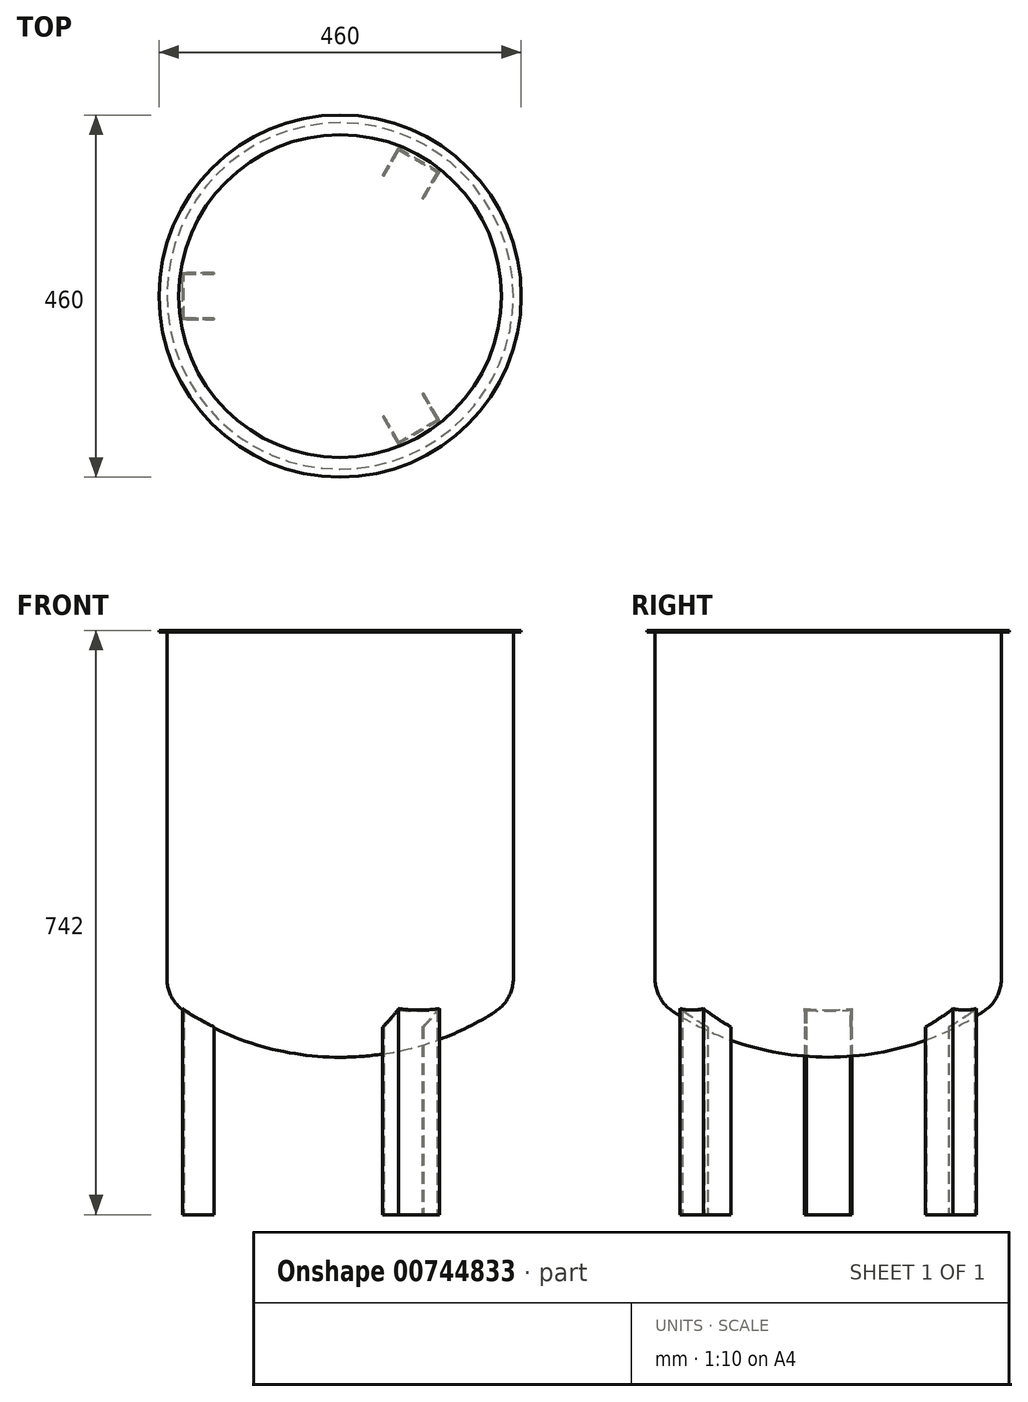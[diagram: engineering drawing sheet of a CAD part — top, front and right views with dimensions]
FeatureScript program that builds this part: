
annotation { "Feature Type Name" : "Feature", "Feature Type Description" : "" }
export const myFeature = defineFeature(function(context is Context, id is Id, definition is map)
    precondition{}
    {
        {
            var Q0;
            Q0=qCreatedBy(makeId("Front.planeOp"),FACE);
            var sketch = newSketch(context, id + "F0", { "sketchPlane" : qUnion([Q0])});
            skLineSegment(sketch, "E0", {"start": v(-220, 100) * mm, "end": v(-220, 540) * mm});
            skArc(sketch, "E1", {"start": v(0, 640) * mm, "mid": v(-102.7, 625.2) * mm, "end": v(-197.07, 582.04) * mm});
            skLineSegment(sketch, "E2", {"start": v(0, 640) * mm, "end": v(58.23, 640) * mm, "construction": true});
            skPoint(sketch, "E3.visualSharp", {"position": v(-220, 566) * mm});
            skArc(sketch, "E3.filletArc", {"start": v(-197.07, 582.04) * mm, "mid": v(-213.9, 563.94) * mm, "end": v(-220, 540) * mm});
            skArc(sketch, "E4", {"start": v(-197.07, 57.96) * mm, "mid": v(-102.7, 14.8) * mm, "end": v(0, 0) * mm});
            skPoint(sketch, "E5.visualSharp", {"position": v(-220, 74) * mm});
            skArc(sketch, "E5.filletArc", {"start": v(-220, 100) * mm, "mid": v(-213.9, 76.06) * mm, "end": v(-197.07, 57.96) * mm});
            skLineSegment(sketch, "E6", {"start": v(0, 0) * mm, "end": v(49.75, 0) * mm, "construction": true});
            skLineSegment(sketch, "E7", {"start": v(0, 640) * mm, "end": v(0, 0) * mm});
            skLineSegment(sketch, "E8", {"start": v(0, 640) * mm, "end": v(0, 722.44) * mm, "construction": true});
            skSolve(sketch);
        }
        {
            var Q0;
            Q0=makeQuery(id+"F0.imprint","IMPRINT",FACE,{"disambiguationData":[TD([[makeQuery(id+"F0.imprint","IMPRINT",EDGE,{"derivedFrom":sQuery(id+"F0.wireOp",EDGE,"E0")}),-1.0]])]});
            var Q1;
            Q1=sQuery(id+"F0.wireOp",EDGE,"E8");
            revolve(context, id + "F1", {"surfaceOperationType" : NewSurfaceOperationType.NEW, "entities" : qUnion([Q0]), "axis" : qUnion([Q1]), "revolveType" : RevolveType.FULL});
        }
        {
            var Q0;
            Q0=qCreatedBy(makeId("Top.planeOp"),FACE);
            var sketch = newSketch(context, id + "F2", { "sketchPlane" : qUnion([Q0])});
            skLineSegment(sketch, "E9", {"start": v(-160, -30) * mm, "end": v(-200, -30) * mm});
            skLineSegment(sketch, "E10", {"start": v(-200, -30) * mm, "end": v(-200, 30) * mm});
            skLineSegment(sketch, "E11", {"start": v(-200, 30) * mm, "end": v(-160, 30) * mm});
            skLineSegment(sketch, "E12", {"start": v(-200, 0) * mm, "end": v(0, 0) * mm, "construction": true});
            skLineSegment(sketch, "E13.0", {"start": v(-198, 28) * mm, "end": v(-160, 28) * mm});
            skLineSegment(sketch, "E13.1", {"start": v(-198, -28) * mm, "end": v(-198, 28) * mm});
            skLineSegment(sketch, "E13.2", {"start": v(-160, -28) * mm, "end": v(-198, -28) * mm});
            skLineSegment(sketch, "E14", {"start": v(-160, -28) * mm, "end": v(-160, -30) * mm});
            skLineSegment(sketch, "E15", {"start": v(-160, 30) * mm, "end": v(-160, 28) * mm});
            skLineSegment(sketch, "E16.1.0", {"start": v(104.25, -124.56) * mm, "end": v(123.25, -157.47) * mm});
            skLineSegment(sketch, "E16.1.1", {"start": v(123.25, -157.47) * mm, "end": v(74.75, -185.47) * mm});
            skLineSegment(sketch, "E16.1.2", {"start": v(74.75, -185.47) * mm, "end": v(55.75, -152.56) * mm});
            skLineSegment(sketch, "E16.1.3", {"start": v(125.98, -158.2) * mm, "end": v(74.02, -188.2) * mm});
            skLineSegment(sketch, "E16.1.4", {"start": v(74.02, -188.2) * mm, "end": v(54.02, -153.56) * mm});
            skLineSegment(sketch, "E16.1.5", {"start": v(105.98, -123.56) * mm, "end": v(125.98, -158.2) * mm});
            skLineSegment(sketch, "E16.1.6", {"start": v(54.02, -153.56) * mm, "end": v(55.75, -152.56) * mm});
            skLineSegment(sketch, "E16.1.7", {"start": v(104.25, -124.56) * mm, "end": v(105.98, -123.56) * mm});
            skLineSegment(sketch, "E16.2.0", {"start": v(55.75, 152.56) * mm, "end": v(74.75, 185.47) * mm});
            skLineSegment(sketch, "E16.2.1", {"start": v(74.75, 185.47) * mm, "end": v(123.25, 157.47) * mm});
            skLineSegment(sketch, "E16.2.2", {"start": v(123.25, 157.47) * mm, "end": v(104.25, 124.56) * mm});
            skLineSegment(sketch, "E16.2.3", {"start": v(74.02, 188.2) * mm, "end": v(125.98, 158.2) * mm});
            skLineSegment(sketch, "E16.2.4", {"start": v(125.98, 158.2) * mm, "end": v(105.98, 123.56) * mm});
            skLineSegment(sketch, "E16.2.5", {"start": v(54.02, 153.56) * mm, "end": v(74.02, 188.2) * mm});
            skLineSegment(sketch, "E16.2.6", {"start": v(105.98, 123.56) * mm, "end": v(104.25, 124.56) * mm});
            skLineSegment(sketch, "E16.2.7", {"start": v(55.75, 152.56) * mm, "end": v(54.02, 153.56) * mm});
            skPoint(sketch, "E16.center", {"position": v(0, 0) * mm});
            skSolve(sketch);
        }
        {
            var Q0;
            Q0=qSketchRegion(id+"F2",true);
            var Q1;
            Q1=makeQuery(id+"F1.opRevolve","SWEPT_BODY",BODY,{"disambiguationData":[OSD([sQuery(id+"F0.wireOp",EDGE,"E0"),sQuery(id+"F0.wireOp",EDGE,"E1"),sQuery(id+"F0.wireOp",EDGE,"E3.filletArc"),sQuery(id+"F0.wireOp",EDGE,"E4"),sQuery(id+"F0.wireOp",EDGE,"E5.filletArc"),sQuery(id+"F0.wireOp",EDGE,"E7")])]});
            extrude(context, id + "F3", {"entities" : qUnion([Q0]), "operationType" : NewBodyOperationType.ADD, "endBound" : BoundingType.UP_TO_BODY, "depth" : 25 * mm, "endBoundEntityBody" : qUnion([Q1]), "offsetDistance" : 25 * mm, "hasSecondDirection" : true, "secondDirectionOppositeDirection" : true, "secondDirectionDepth" : 200 * mm});
        }
        {
            var Q0;
            Q0=qCreatedBy(makeId("Front.planeOp"),FACE);
            var sketch = newSketch(context, id + "F4", { "sketchPlane" : qUnion([Q0])});
            skLineSegment(sketch, "E17.bottom", {"start": v(-259.87, 734.34) * mm, "end": v(282.41, 734.34) * mm});
            skLineSegment(sketch, "E17.top", {"start": v(-259.87, 540) * mm, "end": v(282.41, 540) * mm});
            skLineSegment(sketch, "E17.left", {"start": v(-259.87, 734.34) * mm, "end": v(-259.87, 540) * mm});
            skLineSegment(sketch, "E17.right", {"start": v(282.41, 734.34) * mm, "end": v(282.41, 540) * mm});
            skArc(sketch, "E18", {"start": v(197.07, 582.04) * mm, "mid": v(0, 640) * mm, "end": v(-197.07, 582.04) * mm});
            skPoint(sketch, "E19", {"position": v(0, 640) * mm});
            skSolve(sketch);
        }
        {
            var Q0;
            Q0 = qSketchRegion(id + "F4", true);
            extrude(context, id + "F5", {"entities" : qUnion([Q0]), "operationType" : NewBodyOperationType.REMOVE, "endBound" : BoundingType.THROUGH_ALL, "oppositeDirection" : true, "depth" : 25 * mm, "offsetDistance" : 25 * mm, "hasSecondDirection" : true, "secondDirectionBound" : SecondDirectionBoundingType.THROUGH_ALL, "secondDirectionOppositeDirection" : false, "secondDirectionDepth" : 25 * mm});
        }
        {
            var Q0;
            Q0=makeQuery(id+"F5.boolean.opBoolean","COPY",FACE,{"derivedFrom":makeQuery(id+"F5.opExtrude","SWEPT_FACE",FACE,{"disambiguationData":[OSD([sQuery(id+"F4.wireOp",EDGE,"E17.top")])]})});
            var sketch = newSketch(context, id + "F6", { "sketchPlane" : qUnion([Q0])});
            skCircle(sketch, "E20", {"center": v(0, 0) * mm, "radius": 230 * mm});
            skCircle(sketch, "E21", {"center": v(0, 0) * mm, "radius": 205 * mm});
            skSolve(sketch);
        }
        {
            var Q0;
            Q0 = qSketchRegion(id + "F6", true);
            extrude(context, id + "F7", {"entities" : qUnion([Q0]), "operationType" : NewBodyOperationType.ADD, "depth" : 2 * mm, "offsetDistance" : 25 * mm});
        }
    });
